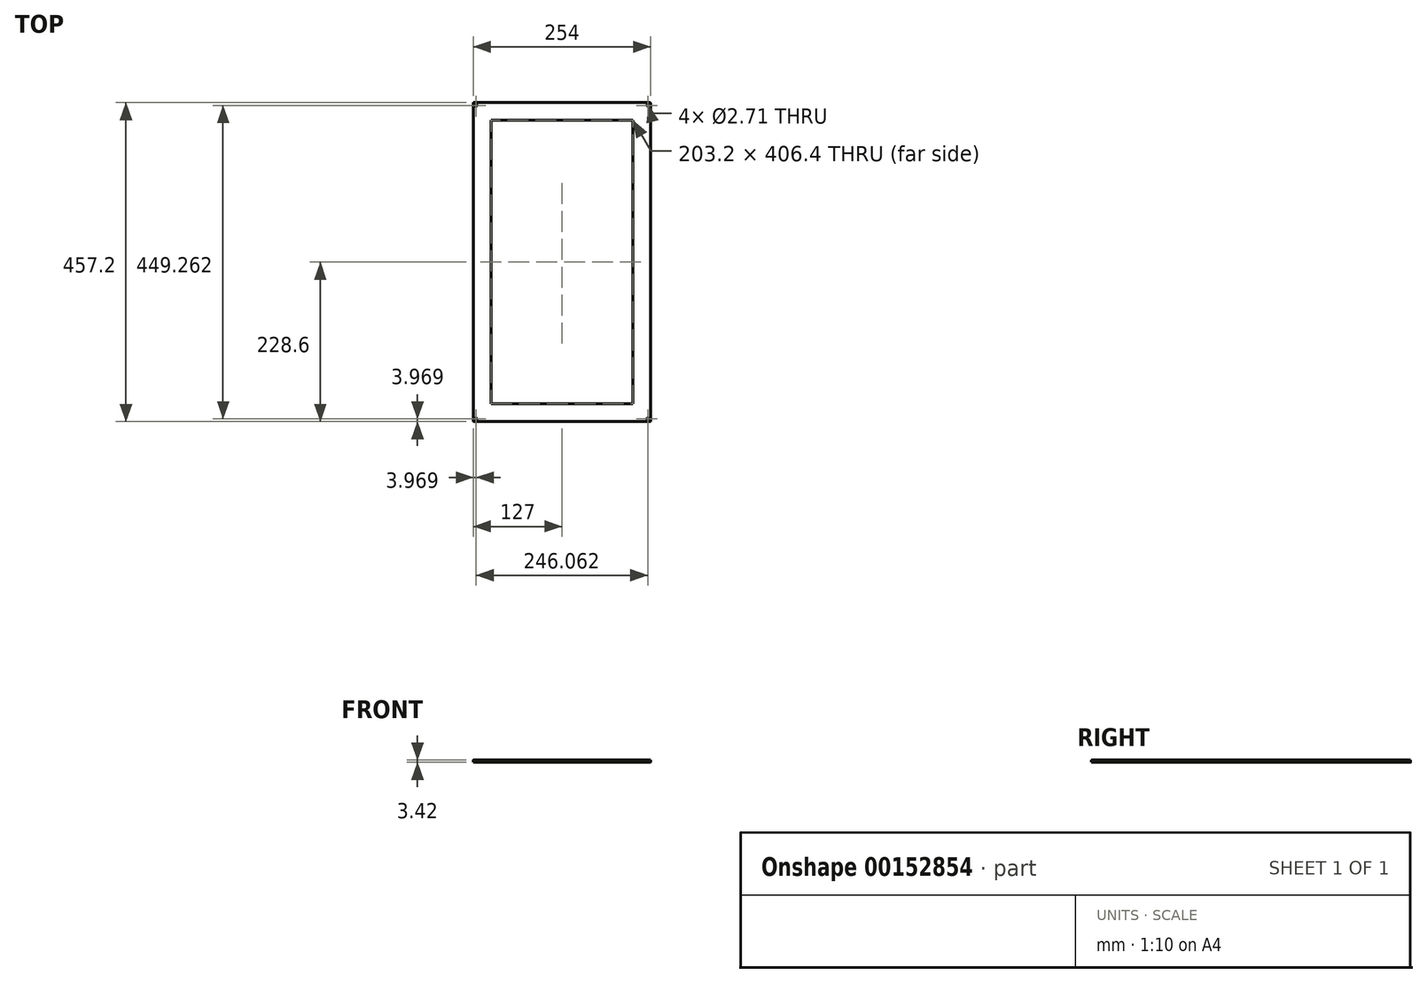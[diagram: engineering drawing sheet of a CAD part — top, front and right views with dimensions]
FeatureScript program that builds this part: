
annotation { "Feature Type Name" : "Feature", "Feature Type Description" : "" }
export const myFeature = defineFeature(function(context is Context, id is Id, definition is map)
    precondition{}
    {
        {
            var Q0;
            Q0=qCreatedBy(makeId("Top.planeOp"),FACE);
            var sketch = newSketch(context, id + "F0", { "sketchPlane" : qUnion([Q0])});
            skLineSegment(sketch, "E0.bottom", {"start": v(127, -228.6) * mm, "end": v(-127, -228.6) * mm});
            skLineSegment(sketch, "E0.top", {"start": v(127, 228.6) * mm, "end": v(-127, 228.6) * mm});
            skLineSegment(sketch, "E0.left", {"start": v(127, -228.6) * mm, "end": v(127, 228.6) * mm});
            skLineSegment(sketch, "E0.right", {"start": v(-127, -228.6) * mm, "end": v(-127, 228.6) * mm});
            skPoint(sketch, "E0.middle", {"position": v(0, 0) * mm});
            skLineSegment(sketch, "E1.bottom", {"start": v(-123.03, 224.63) * mm, "end": v(123.03, 224.63) * mm, "construction": true});
            skLineSegment(sketch, "E1.top", {"start": v(-123.03, -224.63) * mm, "end": v(123.03, -224.63) * mm, "construction": true});
            skLineSegment(sketch, "E1.left", {"start": v(-123.03, 224.63) * mm, "end": v(-123.03, -224.63) * mm, "construction": true});
            skLineSegment(sketch, "E1.right", {"start": v(123.03, 224.63) * mm, "end": v(123.03, -224.63) * mm, "construction": true});
            skLineSegment(sketch, "E2", {"start": v(-123.03, 224.63) * mm, "end": v(-127, 224.63) * mm, "construction": true});
            skLineSegment(sketch, "E3", {"start": v(-123.03, 224.63) * mm, "end": v(-123.03, 228.6) * mm, "construction": true});
            skCircle(sketch, "E4", {"center": v(-123.03, 224.63) * mm, "radius": 1.35 * mm});
            skCircle(sketch, "E5", {"center": v(123.03, 224.63) * mm, "radius": 1.35 * mm});
            skCircle(sketch, "E6", {"center": v(-123.03, -224.63) * mm, "radius": 1.35 * mm});
            skCircle(sketch, "E7", {"center": v(123.03, -224.63) * mm, "radius": 1.35 * mm});
            skLineSegment(sketch, "E8.bottom", {"start": v(-101.6, 203.2) * mm, "end": v(101.6, 203.2) * mm});
            skLineSegment(sketch, "E8.top", {"start": v(-101.6, -203.2) * mm, "end": v(101.6, -203.2) * mm});
            skLineSegment(sketch, "E8.left", {"start": v(-101.6, 203.2) * mm, "end": v(-101.6, -203.2) * mm});
            skLineSegment(sketch, "E8.right", {"start": v(101.6, 203.2) * mm, "end": v(101.6, -203.2) * mm});
            skLineSegment(sketch, "E9", {"start": v(-101.6, 203.2) * mm, "end": v(-123.03, 203.2) * mm, "construction": true});
            skLineSegment(sketch, "E10", {"start": v(-101.6, 203.2) * mm, "end": v(-101.6, 224.63) * mm, "construction": true});
            skSolve(sketch);
        }
        {
            var Q0;
            Q0=qSketchRegion(id+"F0",true);
            extrude(context, id + "F1", {"entities" : qUnion([Q0]), "depth" : 3.42 * mm});
        }
        {
            var Q0;
            Q0=makeQuery(id+"F1.opExtrude","SWEPT_EDGE",EDGE,{"disambiguationData":[OSD([sQuery(id+"F0.wireOp",EDGE,"E0.top"),sQuery(id+"F0.wireOp",EDGE,"E0.right")])]});
            var Q1;
            Q1=makeQuery(id+"F1.opExtrude","SWEPT_EDGE",EDGE,{"disambiguationData":[OSD([sQuery(id+"F0.wireOp",EDGE,"E0.bottom"),sQuery(id+"F0.wireOp",EDGE,"E0.right")])]});
            var Q2;
            Q2=makeQuery(id+"F1.opExtrude","SWEPT_EDGE",EDGE,{"disambiguationData":[OSD([sQuery(id+"F0.wireOp",EDGE,"E0.bottom"),sQuery(id+"F0.wireOp",EDGE,"E0.left")])]});
            var Q3;
            Q3=makeQuery(id+"F1.opExtrude","SWEPT_EDGE",EDGE,{"disambiguationData":[OSD([sQuery(id+"F0.wireOp",EDGE,"E0.top"),sQuery(id+"F0.wireOp",EDGE,"E0.left")])]});
            fillet(context, id + "F2", {"entities" : qUnion([Q0, Q1, Q2, Q3]), "radius" : 0.76 * mm, "tangentPropagation" : true, "allowEdgeOverflow" : false});
        }
    });
